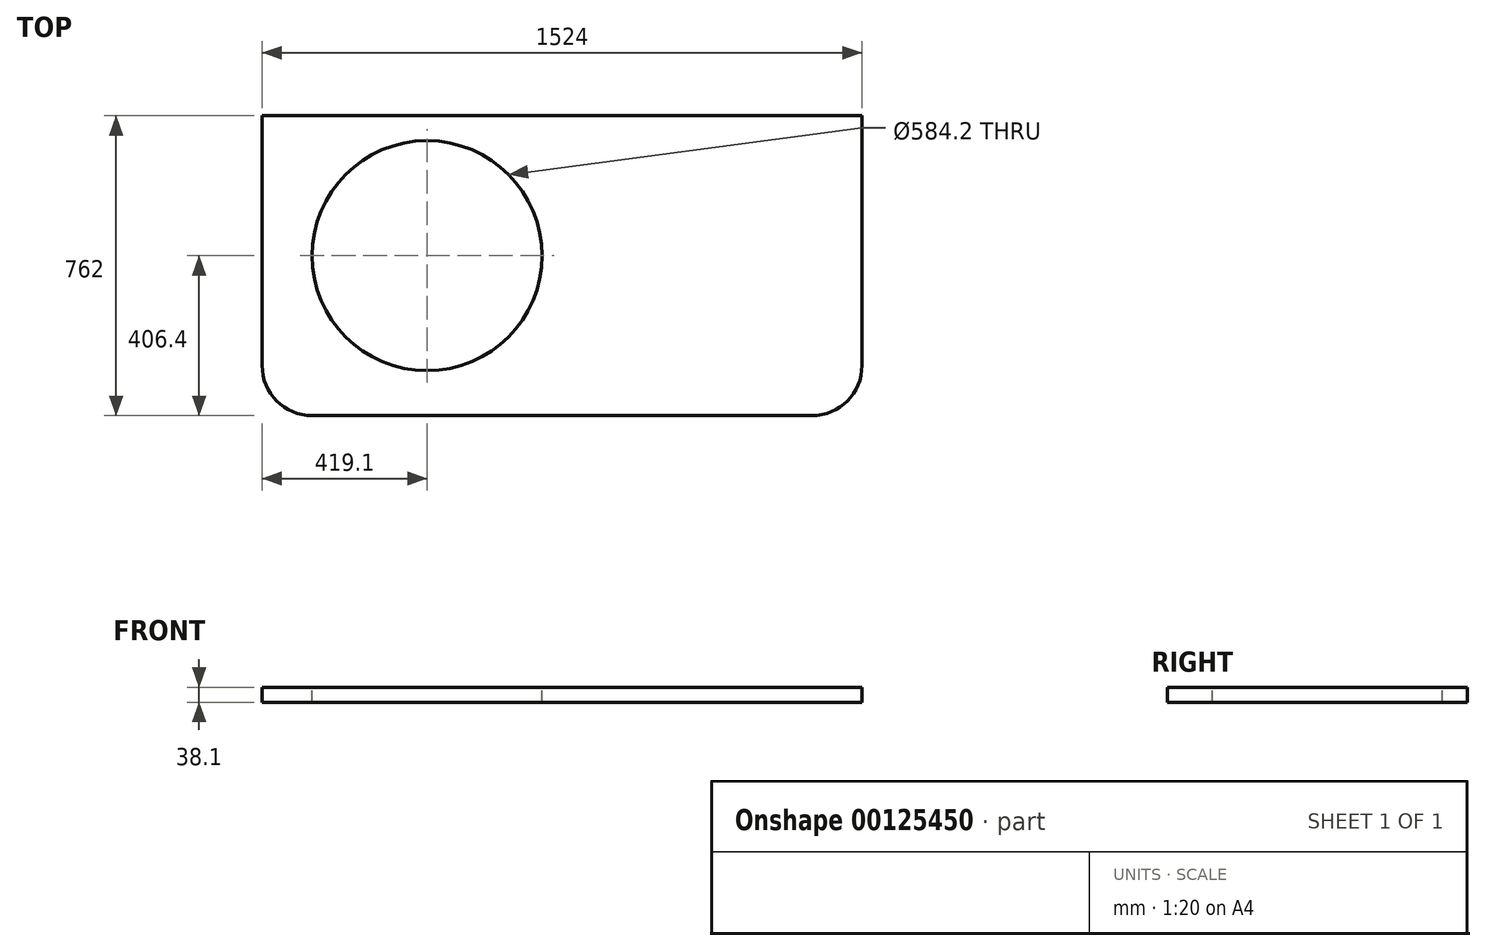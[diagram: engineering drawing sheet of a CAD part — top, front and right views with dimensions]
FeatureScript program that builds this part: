
annotation { "Feature Type Name" : "Feature", "Feature Type Description" : "" }
export const myFeature = defineFeature(function(context is Context, id is Id, definition is map)
    precondition{}
    {
        {
            var Q0;
            Q0=qCreatedBy(makeId("Top.planeOp"),FACE);
            var sketch = newSketch(context, id + "F0", { "sketchPlane" : qUnion([Q0])});
            skLineSegment(sketch, "E0", {"start": v(-762, 0) * mm, "end": v(762, 0) * mm});
            skLineSegment(sketch, "E1", {"start": v(762, 0) * mm, "end": v(762, -635) * mm});
            skLineSegment(sketch, "E2", {"start": v(635, -762) * mm, "end": v(-635, -762) * mm});
            skLineSegment(sketch, "E3", {"start": v(-762, -635) * mm, "end": v(-762, 0) * mm});
            skCircle(sketch, "E4", {"center": v(-342.9, -355.6) * mm, "radius": 292.1 * mm});
            skLineSegment(sketch, "E5", {"start": v(-342.9, -355.6) * mm, "end": v(-762, -355.6) * mm, "construction": true});
            skPoint(sketch, "E6.visualSharp", {"position": v(-762, -762) * mm});
            skArc(sketch, "E6.filletArc", {"start": v(-762, -635) * mm, "mid": v(-724.8, -724.8) * mm, "end": v(-635, -762) * mm});
            skPoint(sketch, "E7.visualSharp", {"position": v(762, -762) * mm});
            skArc(sketch, "E7.filletArc", {"start": v(635, -762) * mm, "mid": v(724.8, -724.8) * mm, "end": v(762, -635) * mm});
            skSolve(sketch);
        }
        {
            var Q0;
            Q0=makeQuery(id+"F0.imprint","IMPRINT",FACE,{"disambiguationData":[TD([[makeQuery(id+"F0.imprint","IMPRINT",EDGE,{"derivedFrom":sQuery(id+"F0.wireOp",EDGE,"E0")}),-1.0]])]});
            extrude(context, id + "F1", {"entities" : qUnion([Q0]), "oppositeDirection" : true, "depth" : 38.1 * mm});
        }
    });
